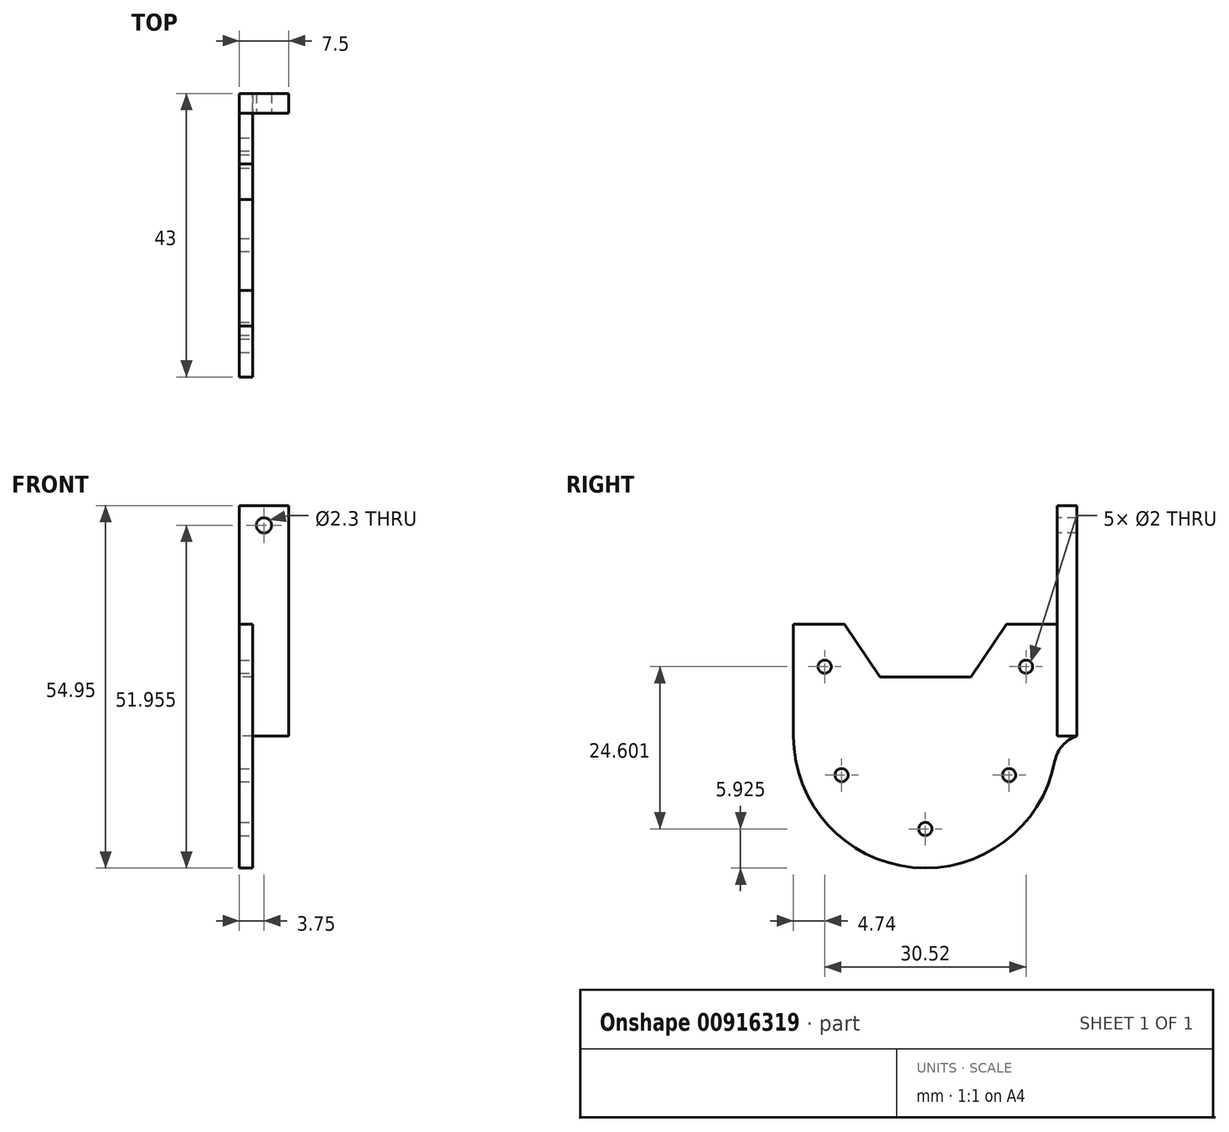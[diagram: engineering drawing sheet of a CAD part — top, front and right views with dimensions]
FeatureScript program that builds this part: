
annotation { "Feature Type Name" : "Feature", "Feature Type Description" : "" }
export const myFeature = defineFeature(function(context is Context, id is Id, definition is map)
    precondition{}
    {
        {
            var Q0;
            Q0=qCreatedBy(makeId("Right.planeOp"),FACE);
            var sketch = newSketch(context, id + "F0", { "sketchPlane" : qUnion([Q0])});
            skLineSegment(sketch, "E0.bottom", {"start": v(20, 8.48) * mm, "end": v(-20, 8.48) * mm});
            skLineSegment(sketch, "E0.left", {"start": v(20, 8.48) * mm, "end": v(20, -8.47) * mm});
            skLineSegment(sketch, "E0.right", {"start": v(-20, 8.48) * mm, "end": v(-20, -8.48) * mm});
            skPoint(sketch, "E0.middle", {"position": v(0, 0) * mm});
            skArc(sketch, "E1", {"start": v(20, -8.47) * mm, "mid": v(0, -28.47) * mm, "end": v(-20, -8.48) * mm});
            skLineSegment(sketch, "E2", {"start": v(-12.3, 8.48) * mm, "end": v(-6.9, 0.47) * mm});
            skLineSegment(sketch, "E3", {"start": v(-6.9, 0.48) * mm, "end": v(0, 0.48) * mm});
            skLineSegment(sketch, "E4", {"start": v(0, 8.48) * mm, "end": v(0, 0.48) * mm, "construction": true});
            skLineSegment(sketch, "E5.MirrorCS", {"start": v(6.9, 0.47) * mm, "end": v(0, 0.48) * mm});
            skLineSegment(sketch, "E6.MirrorCS", {"start": v(12.3, 8.48) * mm, "end": v(6.9, 0.48) * mm});
            skSolve(sketch);
        }
        {
            var Q0;
            {var subQ1=sQuery(id+"F0.wireOp",EDGE,"E0.left");Q0=makeQuery(id+"F0.imprint","IMPRINT",FACE,{"disambiguationData":[TD([[makeQuery(id+"F0.imprint","IMPRINT",EDGE,{"derivedFrom":subQ1}),-1.0]])]});}
            extrude(context, id + "F1", {"entities" : qUnion([Q0]), "depth" : 2 * mm, "offsetDistance" : 25 * mm});
        }
        {
            var Q0;
            Q0=makeQuery(id+"F1.opExtrude","CAP_FACE",FACE,{"disambiguationData":[OSD([sQuery(id+"F0.wireOp",EDGE,"E0.bottom"),sQuery(id+"F0.wireOp",EDGE,"E0.left"),sQuery(id+"F0.wireOp",EDGE,"E0.right"),sQuery(id+"F0.wireOp",EDGE,"E1"),sQuery(id+"F0.wireOp",EDGE,"E2"),sQuery(id+"F0.wireOp",EDGE,"E3"),sQuery(id+"F0.wireOp",EDGE,"E5.MirrorCS"),sQuery(id+"F0.wireOp",EDGE,"E6.MirrorCS")])],"isStart":false});
            var sketch = newSketch(context, id + "F2", { "sketchPlane" : qUnion([Q0])});
            skCircle(sketch, "E7", {"center": v(0, -22.56) * mm, "radius": 1 * mm});
            skCircle(sketch, "E8", {"center": v(-12.7, -14.4) * mm, "radius": 1 * mm});
            skCircle(sketch, "E9", {"center": v(-15.26, 2.05) * mm, "radius": 1 * mm});
            skLineSegment(sketch, "E10", {"start": v(0, -22.56) * mm, "end": v(0, -4.95) * mm, "construction": true});
            skCircle(sketch, "E11.MirrorC", {"center": v(12.7, -14.4) * mm, "radius": 1 * mm});
            skCircle(sketch, "E12.MirrorC", {"center": v(15.26, 2.05) * mm, "radius": 1 * mm});
            skSolve(sketch);
        }
        {
            var Q0;
            Q0 = qSketchRegion(id + "F2", true);
            extrude(context, id + "F3", {"entities" : qUnion([Q0]), "operationType" : NewBodyOperationType.REMOVE, "oppositeDirection" : true, "depth" : 25 * mm, "offsetDistance" : 25 * mm});
        }
        {
            var Q0;
            Q0=makeQuery(id+"F1.opExtrude","SWEPT_FACE",FACE,{"disambiguationData":[OSD([sQuery(id+"F0.wireOp",EDGE,"E0.left")])]});
            var sketch = newSketch(context, id + "F4", { "sketchPlane" : qUnion([Q0])});
            skLineSegment(sketch, "E13.top", {"start": v(0, 26.48) * mm, "end": v(-7.5, 26.48) * mm});
            skLineSegment(sketch, "E13.left", {"start": v(0, 8.48) * mm, "end": v(0, 26.48) * mm});
            skLineSegment(sketch, "E13.right", {"start": v(-7.5, 8.47) * mm, "end": v(-7.5, 26.48) * mm});
            skLineSegment(sketch, "E14.bottom", {"start": v(-7.5, 8.48) * mm, "end": v(0, 8.48) * mm, "construction": true});
            skLineSegment(sketch, "E14.top", {"start": v(-7.5, -8.47) * mm, "end": v(0, -8.47) * mm});
            skLineSegment(sketch, "E14.left", {"start": v(-7.5, 8.47) * mm, "end": v(-7.5, -8.47) * mm});
            skLineSegment(sketch, "E14.right", {"start": v(0, 8.48) * mm, "end": v(0, -8.47) * mm});
            skCircle(sketch, "E15", {"center": v(-3.75, 23.48) * mm, "radius": 1.15 * mm});
            skLineSegment(sketch, "E16", {"start": v(-3.75, 26.48) * mm, "end": v(-3.75, 23.48) * mm, "construction": true});
            skLineSegment(sketch, "E17", {"start": v(-2, -8.47) * mm, "end": v(-7.5, 8.47) * mm});
            skSolve(sketch);
        }
        {
            var Q0;
            Q0 = qSketchRegion(id + "F4", true);
            extrude(context, id + "F5", {"entities" : qUnion([Q0]), "operationType" : NewBodyOperationType.ADD, "depth" : 3 * mm, "offsetDistance" : 25 * mm});
        }
        {
            var Q0;
            Q0=makeQuery(id+"F5.boolean.opBoolean","MERGE",EDGE,{"derivedFrom":[makeQuery(id+"F1.opExtrude","SWEPT_EDGE",EDGE,{"disambiguationData":[OSD([sQuery(id+"F0.wireOp",EDGE,"E0.left"),sQuery(id+"F0.wireOp",EDGE,"E1")])]}),makeQuery(id+"F5.opExtrude","CAP_EDGE",EDGE,{"disambiguationData":[OSD([sQuery(id+"F4.wireOp",EDGE,"E14.top")])],"isStart":true})]});
            fillet(context, id + "F6", {"entities" : qUnion([Q0]), "radius" : 5 * mm, "tangentPropagation" : true, "allowEdgeOverflow" : false});
        }
    });
